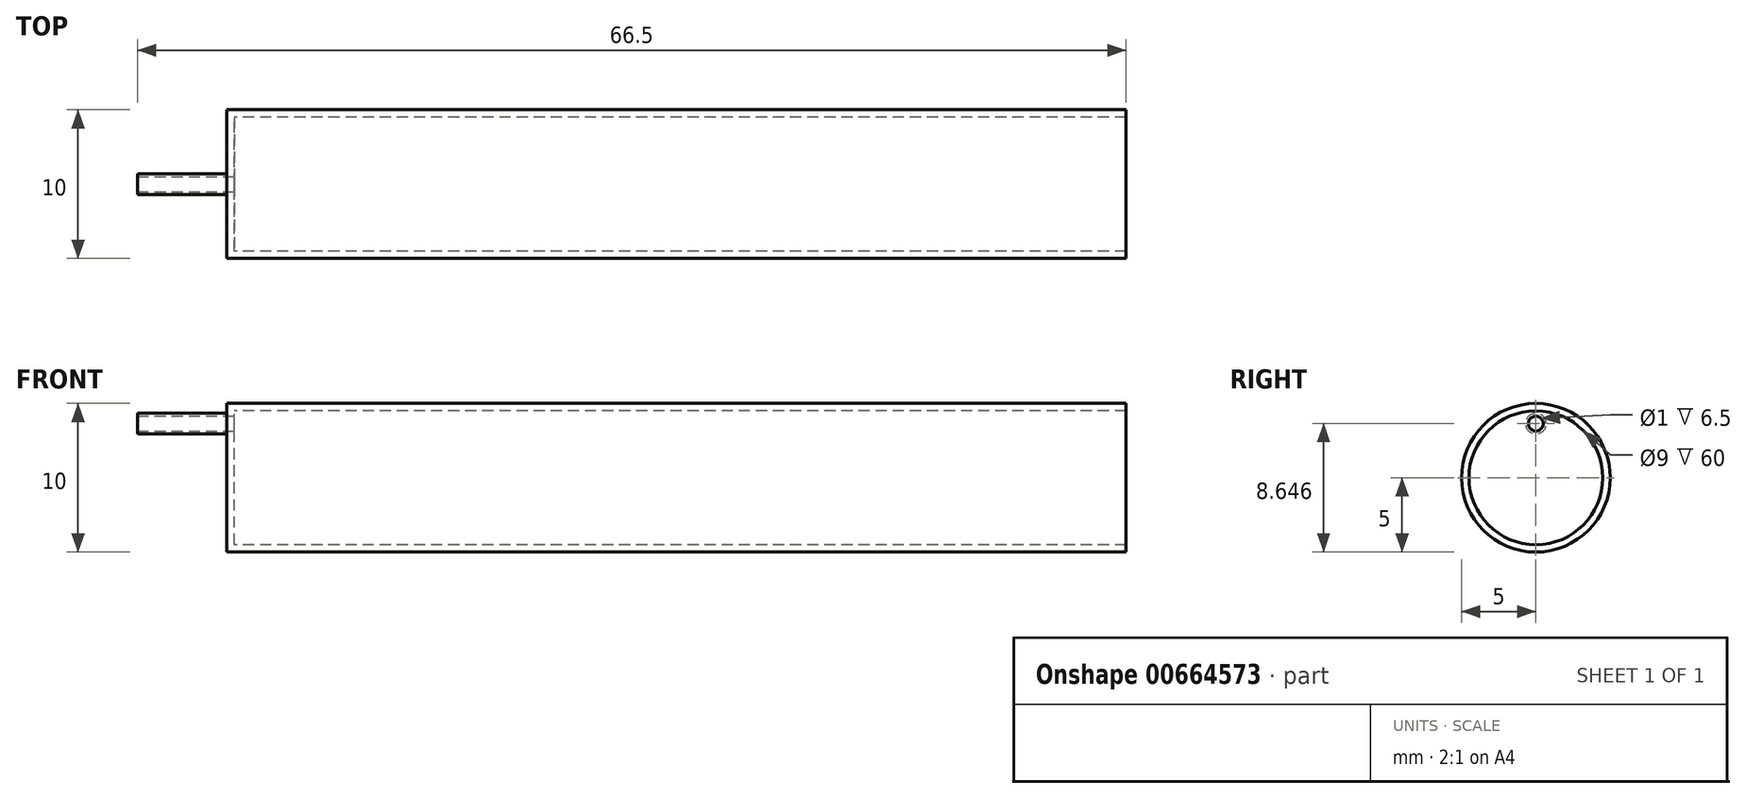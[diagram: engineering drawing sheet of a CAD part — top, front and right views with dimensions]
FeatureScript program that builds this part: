
annotation { "Feature Type Name" : "Feature", "Feature Type Description" : "" }
export const myFeature = defineFeature(function(context is Context, id is Id, definition is map)
    precondition{}
    {
        {
            var Q0;
            Q0=qCreatedBy(makeId("Right.planeOp"),FACE);
            var sketch = newSketch(context, id + "F0", { "sketchPlane" : qUnion([Q0])});
            skCircle(sketch, "E0", {"center": v(0, 0) * mm, "radius": 4.5 * mm});
            skCircle(sketch, "E1", {"center": v(0, 0) * mm, "radius": 5 * mm});
            skCircle(sketch, "E2", {"center": v(0, 3.65) * mm, "radius": 0.5 * mm});
            skSolve(sketch);
        }
        {
            var Q0;
            Q0=makeQuery(id+"F0.imprint","IMPRINT",FACE,{"disambiguationData":[TD([[makeQuery(id+"F0.imprint","IMPRINT",EDGE,{"derivedFrom":sQuery(id+"F0.wireOp",EDGE,"E0")}),-1.0]])]});
            var Q1;
            Q1=makeQuery(id+"F0.imprint","IMPRINT",FACE,{"disambiguationData":[TD([[makeQuery(id+"F0.imprint","IMPRINT",EDGE,{"derivedFrom":sQuery(id+"F0.wireOp",EDGE,"E0")}),1.0]])]});
            extrude(context, id + "F1", {"entities" : qUnion([Q0, Q1]), "oppositeDirection" : true, "depth" : .5 * mm, "offsetDistance" : 25 * mm});
        }
        {
            var Q0;
            Q0=makeQuery(id+"F1.opExtrude","CAP_FACE",FACE,{"disambiguationData":[OSD([sQuery(id+"F0.wireOp",EDGE,"E1"),sQuery(id+"F0.wireOp",EDGE,"E2")])],"isStart":false});
            var sketch = newSketch(context, id + "F2", { "sketchPlane" : qUnion([Q0])});
            skCircle(sketch, "E3", {"center": v(0, 3.65) * mm, "radius": 0.7 * mm});
            skSolve(sketch);
        }
        {
            var Q0;
            Q0=makeQuery(id+"F2.imprint","IMPRINT",FACE,{"disambiguationData":[TD([[makeQuery(id+"F2.imprint","IMPRINT",EDGE,{"derivedFrom":sQuery(id+"F2.wireOp",EDGE,"E3")}),1.0]])]});
            extrude(context, id + "F3", {"entities" : qUnion([Q0]), "operationType" : NewBodyOperationType.ADD, "depth" : 6 * mm, "offsetDistance" : 25 * mm});
        }
        {
            var Q0;
            Q0=makeQuery(id+"F0.imprint","IMPRINT",FACE,{"disambiguationData":[TD([[makeQuery(id+"F0.imprint","IMPRINT",EDGE,{"derivedFrom":sQuery(id+"F0.wireOp",EDGE,"E0")}),-1.0]])]});
            extrude(context, id + "F4", {"entities" : qUnion([Q0]), "operationType" : NewBodyOperationType.ADD, "depth" : 60 * mm, "offsetDistance" : 25 * mm});
        }
    });
